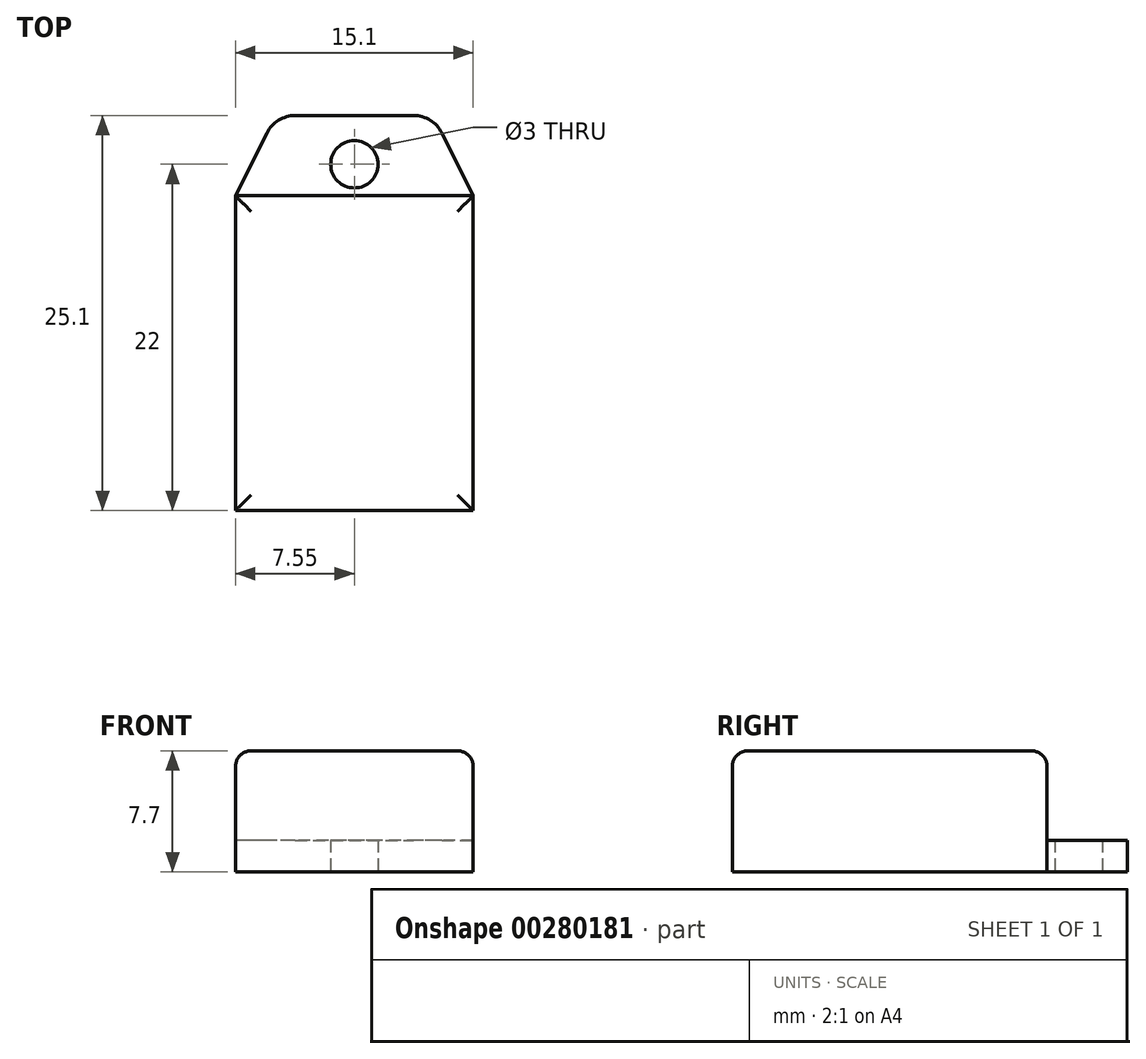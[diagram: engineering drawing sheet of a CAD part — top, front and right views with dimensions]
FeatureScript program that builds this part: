
annotation { "Feature Type Name" : "Feature", "Feature Type Description" : "" }
export const myFeature = defineFeature(function(context is Context, id is Id, definition is map)
    precondition{}
    {
        {
            var Q0;
            Q0=qCreatedBy(makeId("Top.planeOp"),FACE);
            var sketch = newSketch(context, id + "F0", { "sketchPlane" : qUnion([Q0])});
            skLineSegment(sketch, "E0.bottom", {"start": v(7.55, -10) * mm, "end": v(-7.55, -10) * mm});
            skLineSegment(sketch, "E0.top", {"start": v(7.55, 10) * mm, "end": v(-7.55, 10) * mm});
            skLineSegment(sketch, "E0.left", {"start": v(7.55, -10) * mm, "end": v(7.55, 10) * mm});
            skLineSegment(sketch, "E0.right", {"start": v(-7.55, -10) * mm, "end": v(-7.55, 10) * mm});
            skPoint(sketch, "E0.middle", {"position": v(0, 0) * mm});
            skLineSegment(sketch, "E1", {"start": v(-3.76, 15.1) * mm, "end": v(3.76, 15.1) * mm});
            skLineSegment(sketch, "E2", {"start": v(-5.55, 14) * mm, "end": v(-7.55, 10) * mm});
            skLineSegment(sketch, "E3", {"start": v(5.55, 14) * mm, "end": v(7.55, 10) * mm});
            skPoint(sketch, "E4.visualSharp", {"position": v(-5, 15.1) * mm});
            skArc(sketch, "E4.filletArc", {"start": v(-3.76, 15.1) * mm, "mid": v(-4.82, 14.8) * mm, "end": v(-5.55, 14) * mm});
            skPoint(sketch, "E5.visualSharp", {"position": v(5, 15.1) * mm});
            skArc(sketch, "E5.filletArc", {"start": v(5.55, 14) * mm, "mid": v(4.82, 14.8) * mm, "end": v(3.76, 15.1) * mm});
            skCircle(sketch, "E6", {"center": v(0, 12) * mm, "radius": 1.5 * mm});
            skSolve(sketch);
        }
        {
            var Q0;
            Q0=makeQuery(id+"F0.imprint","IMPRINT",FACE,{"disambiguationData":[TD([[makeQuery(id+"F0.imprint","IMPRINT",EDGE,{"derivedFrom":sQuery(id+"F0.wireOp",EDGE,"E0.top")}),-1.0]])]});
            extrude(context, id + "F1", {"entities" : qUnion([Q0]), "depth" : 2 * mm});
        }
        {
            var Q0;
            Q0=makeQuery(id+"F0.imprint","IMPRINT",FACE,{"disambiguationData":[TD([[makeQuery(id+"F0.imprint","IMPRINT",EDGE,{"derivedFrom":sQuery(id+"F0.wireOp",EDGE,"E0.bottom")}),-1.0]])]});
            extrude(context, id + "F2", {"entities" : qUnion([Q0]), "operationType" : NewBodyOperationType.ADD, "depth" : 7.7 * mm});
        }
        {
            var Q0;
            Q0=makeQuery(id+"F2.opExtrude","CAP_FACE",FACE,{"disambiguationData":[OSD([sQuery(id+"F0.wireOp",EDGE,"E0.bottom"),sQuery(id+"F0.wireOp",EDGE,"E0.top"),sQuery(id+"F0.wireOp",EDGE,"E0.left"),sQuery(id+"F0.wireOp",EDGE,"E0.right")])],"isStart":false});
            fillet(context, id + "F3", {"entities" : qUnion([Q0]), "radius" : 1 * mm, "tangentPropagation" : true, "allowEdgeOverflow" : false});
        }
    });
